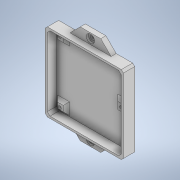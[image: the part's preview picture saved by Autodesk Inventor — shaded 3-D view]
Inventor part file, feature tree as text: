
AUTODESK INVENTOR PART (.ipt)
format: ipt  version: 2021 (Build 250183000, 183)  size: 532,480 bytes
history: native  units: mm
features: sketch x8, extrude x6, other x4, reference x4, hole x3, mirror x2, chamfer x2, projected_geometry x2, thicken_offset x1, direct_edit x1, move_body x1
ambient origin geometry x8: Origin, YZ Plane, XZ Plane, XY Plane, X Axis, Y Axis, Z Axis, Center Point
bodies: Solid1 (feature_tree)
feature tree (34):
  extrude  "Extrusion1"  Depth=3.0mm
  extrude  "Extrusion2"  Depth=5.0mm
  extrude  "Extrusion3"  Depth=6.0mm TaperAngle=0.0deg
  other  "Work Point1"
  extrude  "Extrusion4"  Depth=10.0mm
  other  "Work Point5"
  hole  "Hole1"  [1 undecoded]
  mirror  "Mirror1"
  chamfer  "Chamfer1"  Distance=10.0mm
  thicken_offset  "Thicken1"
  extrude  "Extrusion5"  Depth=1.0mm
  sketch  "Sketch6"  dims[d14=10.0mm d15=10.0mm d16=3.0mm d17=6.0mm d18=8.0mm d19=3.0mm d20=90.0deg d21=8.0mm d22=20.594885mm d23=10.0mm]
  hole  "Hole4"  [1 undecoded]
  mirror  "Mirror3"
  hole  "Hole5"  [1 undecoded]
  extrude  "Extrusion7"  Depth=10.0mm
  chamfer  "Chamfer2"  Angle=45.0deg  [1 undecoded]
  direct_edit  "Direct Edit1"
  sketch  "Sketch1"  dims[d0=3.0mm d1=3.0mm]
  reference  "Reference1"
  reference  "Reference2"
  reference  "Reference3"
  reference  "Reference4"
  sketch  "Sketch2"  dims[d2=3.0mm d3=5.0mm d4=0.0mm d5=0.0mm d6=70.0mm]
  sketch  "Sketch3"  dims[d7=70.0mm d8=6.0mm d9=0.0mm]
  other  "Work Point2"
  sketch  "Sketch4"  dims[d10=10.0mm d11=10.0mm]
  sketch  "Sketch5"  dims[d12=3.0mm d13=0.0mm]
  sketch  "Sketch8"  dims[d24=10.0mm d25=10.0mm d26=0.0mm]
  sketch  "Sketch9"  dims[d36=2.0mm d37=2.0mm d38=45.0deg d39=1.0mm d40=1.0mm d41=20.0mm d42=10.0mm d43=45.0deg d44=10.0mm d45=0.0mm d55=4.2mm d56=6.0mm d57=8.0mm d58=2.0mm d59=90.0deg d60=8.0mm d61=20.594885mm d64=60.0mm d65=30.0mm d66=30.0mm d67=3.0mm d68=6.0mm d69=4.0mm d70=2.0mm d71=90.0deg d72=8.0mm d73=20.594885mm d74=3.5mm d75=3.5mm d76=10.0mm d77=0.0mm d78=1.5mm d79=2.0mm d80=45.0deg d81=3.5mm d82=3.5mm d83=0.0mm d84=0.0mm d85=3.0mm]
  projected_geometry  "Projected Loop2"
  projected_geometry  "Projected Loop3"
  other  "battery_protection_battery-protection.iam"
  move_body  "Move1"
note: 4 required parameter values undecoded (feature->parameter linkage not recoverable at this tier; creation-order binding heuristic only, values carry confidence <= 0.55)
